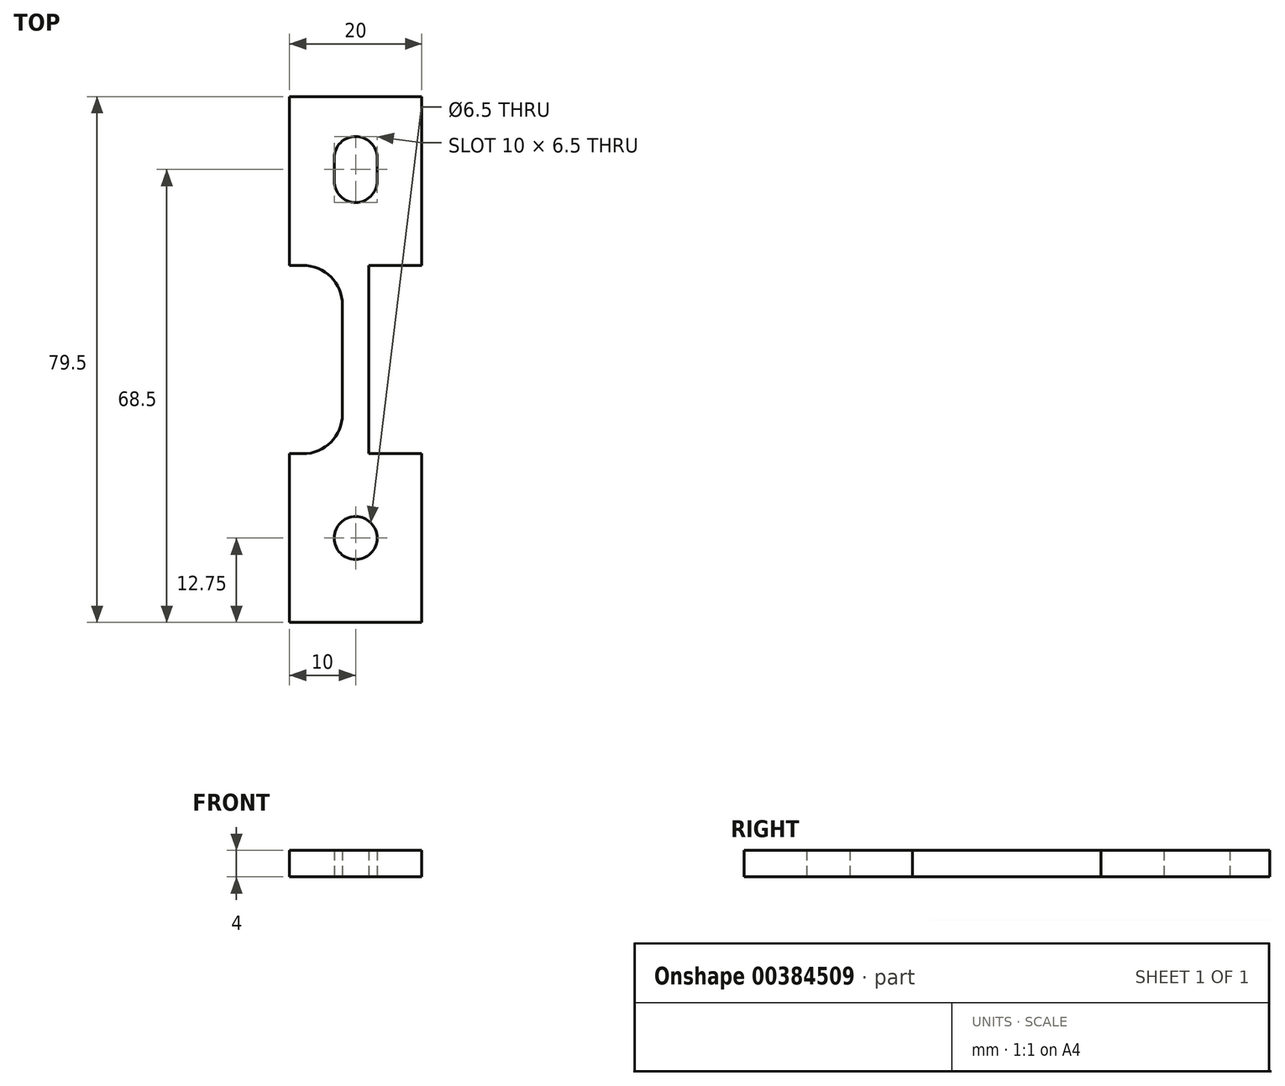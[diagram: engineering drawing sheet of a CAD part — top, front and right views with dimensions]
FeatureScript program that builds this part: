
annotation { "Feature Type Name" : "Feature", "Feature Type Description" : "" }
export const myFeature = defineFeature(function(context is Context, id is Id, definition is map)
    precondition{}
    {
        {
            var Q0;
            Q0=qCreatedBy(makeId("Top.planeOp"),FACE);
            var sketch = newSketch(context, id + "F0", { "sketchPlane" : qUnion([Q0])});
            skLineSegment(sketch, "E0.bottom", {"start": v(-10, 39.75) * mm, "end": v(10, 39.75) * mm});
            skLineSegment(sketch, "E0.top", {"start": v(-10, 14.25) * mm, "end": v(10, 14.25) * mm});
            skLineSegment(sketch, "E0.left", {"start": v(-10, 39.75) * mm, "end": v(-10, 14.25) * mm});
            skLineSegment(sketch, "E0.right", {"start": v(10, 39.75) * mm, "end": v(10, 14.25) * mm});
            skLineSegment(sketch, "E1", {"start": v(0, 30.5) * mm, "end": v(0, 27) * mm, "construction": true});
            skPoint(sketch, "E1.endSnap0", {"position": v(0, 28.75) * mm});
            skArc(sketch, "E2.0.startCap", {"start": v(-3.25, 30.5) * mm, "mid": v(0, 33.75) * mm, "end": v(3.25, 30.5) * mm});
            skArc(sketch, "E2.0.endCap", {"start": v(3.25, 27) * mm, "mid": v(0, 23.75) * mm, "end": v(-3.25, 27) * mm});
            skLineSegment(sketch, "E2.0.left", {"start": v(3.25, 30.5) * mm, "end": v(3.25, 27) * mm});
            skLineSegment(sketch, "E2.0.right", {"start": v(-3.25, 30.5) * mm, "end": v(-3.25, 27) * mm});
            skCircle(sketch, "E3", {"center": v(0, -27) * mm, "radius": 3.25 * mm});
            skLineSegment(sketch, "E4.bottom", {"start": v(-10, -39.75) * mm, "end": v(10, -39.75) * mm});
            skLineSegment(sketch, "E4.top", {"start": v(-10, -14.25) * mm, "end": v(10, -14.25) * mm});
            skLineSegment(sketch, "E4.left", {"start": v(-10, -39.75) * mm, "end": v(-10, -14.25) * mm});
            skLineSegment(sketch, "E4.right", {"start": v(10, -39.75) * mm, "end": v(10, -14.25) * mm});
            skLineSegment(sketch, "E5", {"start": v(-10, -39.75) * mm, "end": v(10, -14.25) * mm, "construction": true});
            skLineSegment(sketch, "E6", {"start": v(0, 23.75) * mm, "end": v(0, 0) * mm, "construction": true});
            skLineSegment(sketch, "E7", {"start": v(0, 0) * mm, "end": v(0, -23.75) * mm, "construction": true});
            skLineSegment(sketch, "E8", {"start": v(0, 23.75) * mm, "end": v(-10, 23.75) * mm, "construction": true});
            skLineSegment(sketch, "E9", {"start": v(-10, 23.75) * mm, "end": v(-10, 14.25) * mm, "construction": true});
            skLineSegment(sketch, "E10", {"start": v(0, -23.75) * mm, "end": v(-10, -23.75) * mm, "construction": true});
            skLineSegment(sketch, "E11", {"start": v(-10, -23.75) * mm, "end": v(-10, -14.25) * mm, "construction": true});
            skSolve(sketch);
        }
        {
            var Q0;
            Q0 = qSketchRegion(id + "F0", true);
            extrude(context, id + "F1", {"entities" : qUnion([Q0]), "depth" : 4 * mm});
        }
        {
            var Q0;
            Q0=qCreatedBy(makeId("Top.planeOp"),FACE);
            var sketch = newSketch(context, id + "F2", { "sketchPlane" : qUnion([Q0])});
            skLineSegment(sketch, "E12.bottom", {"start": v(-2, 14.25) * mm, "end": v(2, 14.25) * mm});
            skLineSegment(sketch, "E12.top", {"start": v(-2, -14.25) * mm, "end": v(2, -14.25) * mm});
            skLineSegment(sketch, "E12.left", {"start": v(-2, 14.25) * mm, "end": v(-2, -14.25) * mm});
            skLineSegment(sketch, "E12.right", {"start": v(2, 14.25) * mm, "end": v(2, -14.25) * mm});
            skLineSegment(sketch, "E13", {"start": v(0, 14.25) * mm, "end": v(0, -14.25) * mm, "construction": true});
            skSolve(sketch);
        }
        {
            var Q0;
            Q0 = qSketchRegion(id + "F2", true);
            extrude(context, id + "F3", {"entities" : qUnion([Q0]), "operationType" : NewBodyOperationType.ADD, "depth" : 4 * mm});
        }
        {
            var Q0;
            Q0=makeQuery(id+"F3.opExtrude","SWEPT_EDGE",EDGE,{"disambiguationData":[OSD([sQuery(id+"F2.wireOp",EDGE,"E12.bottom"),sQuery(id+"F2.wireOp",EDGE,"E12.left")])]});
            var Q1;
            Q1=makeQuery(id+"F3.opExtrude","SWEPT_EDGE",EDGE,{"disambiguationData":[OSD([sQuery(id+"F2.wireOp",EDGE,"E12.bottom"),sQuery(id+"F2.wireOp",EDGE,"E12.right")])]});
            var Q2;
            Q2=makeQuery(id+"F3.opExtrude","SWEPT_EDGE",EDGE,{"disambiguationData":[OSD([sQuery(id+"F2.wireOp",EDGE,"E12.top"),sQuery(id+"F2.wireOp",EDGE,"E12.right")])]});
            var Q3;
            Q3=makeQuery(id+"F3.opExtrude","SWEPT_EDGE",EDGE,{"disambiguationData":[OSD([sQuery(id+"F2.wireOp",EDGE,"E12.top"),sQuery(id+"F2.wireOp",EDGE,"E12.left")])]});
            fillet(context, id + "F4", {"entities" : qUnion([Q0, Q1, Q2, Q3]), "radius" : 6 * mm, "tangentPropagation" : true, "allowEdgeOverflow" : false});
        }
    });
